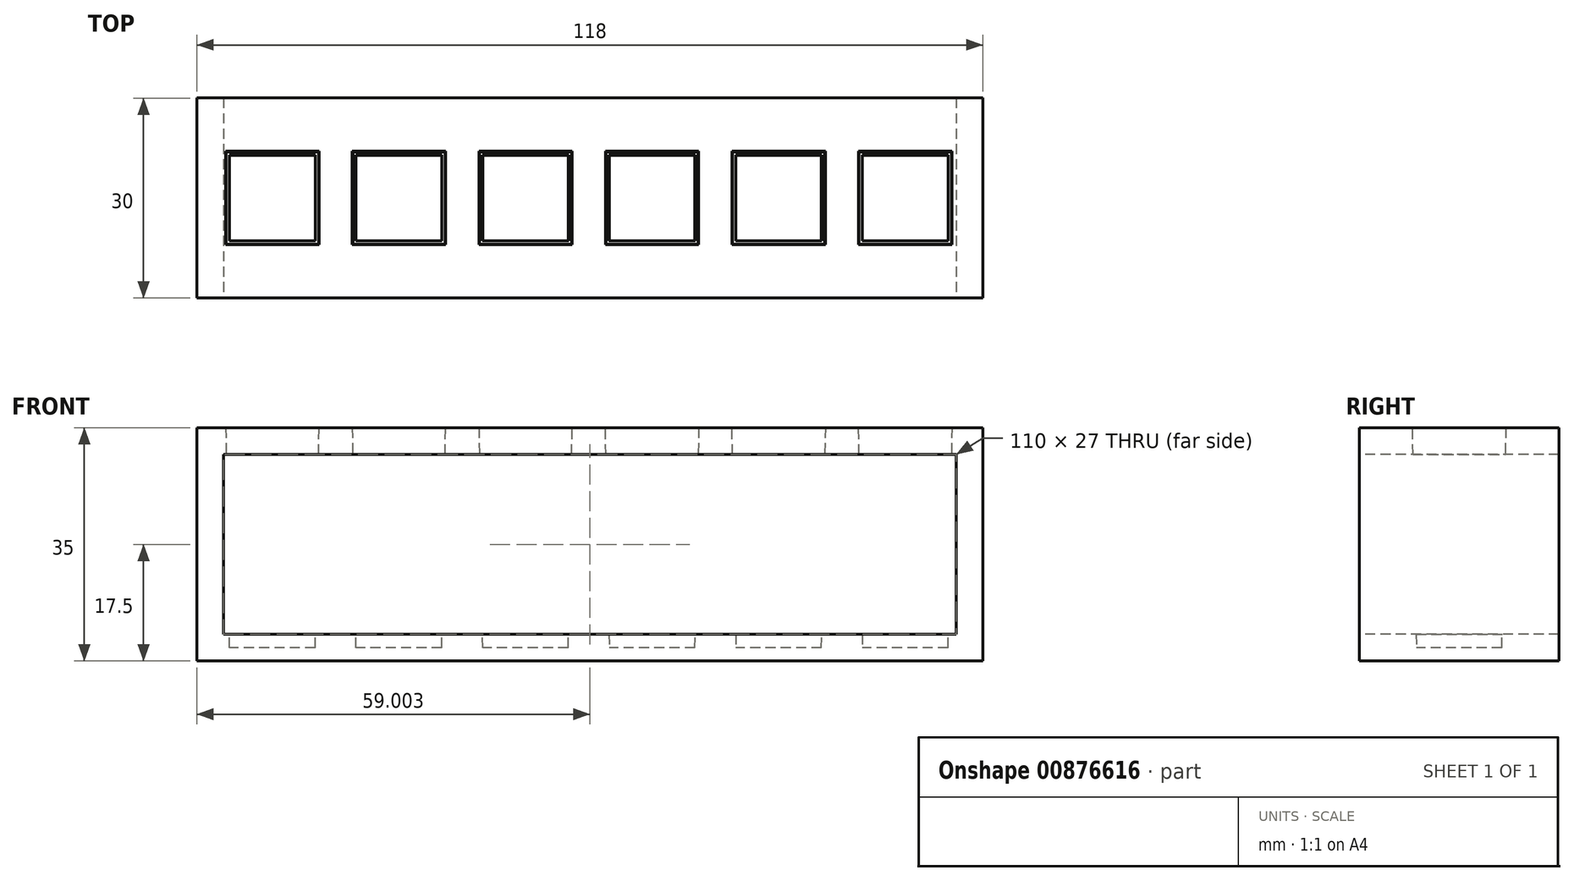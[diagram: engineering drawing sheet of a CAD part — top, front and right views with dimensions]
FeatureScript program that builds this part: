
annotation { "Feature Type Name" : "Feature", "Feature Type Description" : "" }
export const myFeature = defineFeature(function(context is Context, id is Id, definition is map)
    precondition{}
    {
        {
            var Q0;
            Q0=qCreatedBy(makeId("Top.planeOp"),FACE);
            var sketch = newSketch(context, id + "F0", { "sketchPlane" : qUnion([Q0])});
            skLineSegment(sketch, "E0.bottom", {"start": v(-64.3, -10.83) * mm, "end": v(53.7, -10.83) * mm});
            skLineSegment(sketch, "E0.top", {"start": v(-64.3, -40.83) * mm, "end": v(53.7, -40.83) * mm});
            skLineSegment(sketch, "E0.left", {"start": v(-64.3, -10.83) * mm, "end": v(-64.3, -40.83) * mm});
            skLineSegment(sketch, "E0.right", {"start": v(53.7, -10.83) * mm, "end": v(53.7, -40.83) * mm});
            skSolve(sketch);
        }
        {
            var Q0;
            Q0 = qSketchRegion(id + "F0", true);
            extrude(context, id + "F1", {"entities" : qUnion([Q0]), "depth" : 35 * mm, "offsetDistance" : 25 * mm});
        }
        {
            var Q0;
            Q0=makeQuery(id+"F1.opExtrude","CAP_FACE",FACE,{"disambiguationData":[OSD([sQuery(id+"F0.wireOp",EDGE,"E0.bottom"),sQuery(id+"F0.wireOp",EDGE,"E0.top"),sQuery(id+"F0.wireOp",EDGE,"E0.left"),sQuery(id+"F0.wireOp",EDGE,"E0.right")])],"isStart":false});
            var sketch = newSketch(context, id + "F2", { "sketchPlane" : qUnion([Q0])});
            skLineSegment(sketch, "E1.bottom", {"start": v(-59.96, -18.83) * mm, "end": v(-45.96, -18.83) * mm});
            skLineSegment(sketch, "E1.top", {"start": v(-59.96, -32.83) * mm, "end": v(-45.96, -32.83) * mm});
            skLineSegment(sketch, "E1.left", {"start": v(-59.96, -18.83) * mm, "end": v(-59.96, -32.83) * mm});
            skLineSegment(sketch, "E1.right", {"start": v(-45.96, -18.83) * mm, "end": v(-45.96, -32.83) * mm});
            skLineSegment(sketch, "E2.bottom", {"start": v(-40.96, -18.83) * mm, "end": v(-26.96, -18.83) * mm});
            skLineSegment(sketch, "E2.top", {"start": v(-40.96, -32.83) * mm, "end": v(-26.96, -32.83) * mm});
            skLineSegment(sketch, "E2.left", {"start": v(-40.96, -18.83) * mm, "end": v(-40.96, -32.83) * mm});
            skLineSegment(sketch, "E2.right", {"start": v(-26.96, -18.83) * mm, "end": v(-26.96, -32.83) * mm});
            skLineSegment(sketch, "E3.bottom", {"start": v(-21.96, -18.83) * mm, "end": v(-7.96, -18.83) * mm});
            skLineSegment(sketch, "E3.top", {"start": v(-21.96, -32.83) * mm, "end": v(-7.96, -32.83) * mm});
            skLineSegment(sketch, "E3.left", {"start": v(-21.96, -18.83) * mm, "end": v(-21.96, -32.83) * mm});
            skLineSegment(sketch, "E3.right", {"start": v(-7.96, -18.83) * mm, "end": v(-7.96, -32.83) * mm});
            skLineSegment(sketch, "E4.bottom", {"start": v(11.04, -18.83) * mm, "end": v(-2.96, -18.83) * mm});
            skLineSegment(sketch, "E4.top", {"start": v(11.04, -32.83) * mm, "end": v(-2.96, -32.83) * mm});
            skLineSegment(sketch, "E4.left", {"start": v(11.04, -18.83) * mm, "end": v(11.04, -32.83) * mm});
            skLineSegment(sketch, "E4.right", {"start": v(-2.96, -18.83) * mm, "end": v(-2.96, -32.83) * mm});
            skLineSegment(sketch, "E5.bottom", {"start": v(30.04, -18.83) * mm, "end": v(16.04, -18.83) * mm});
            skLineSegment(sketch, "E5.top", {"start": v(30.04, -32.83) * mm, "end": v(16.04, -32.83) * mm});
            skLineSegment(sketch, "E5.left", {"start": v(30.04, -18.83) * mm, "end": v(30.04, -32.83) * mm});
            skLineSegment(sketch, "E5.right", {"start": v(16.04, -18.83) * mm, "end": v(16.04, -32.83) * mm});
            skLineSegment(sketch, "E6.bottom", {"start": v(49.04, -18.83) * mm, "end": v(35.04, -18.83) * mm});
            skLineSegment(sketch, "E6.top", {"start": v(49.04, -32.83) * mm, "end": v(35.04, -32.83) * mm});
            skLineSegment(sketch, "E6.left", {"start": v(49.04, -18.83) * mm, "end": v(49.04, -32.83) * mm});
            skLineSegment(sketch, "E6.right", {"start": v(35.04, -18.83) * mm, "end": v(35.04, -32.83) * mm});
            skSolve(sketch);
        }
        {
            var Q0;
            Q0 = qSketchRegion(id + "F2", true);
            extrude(context, id + "F3", {"entities" : qUnion([Q0]), "operationType" : NewBodyOperationType.REMOVE, "oppositeDirection" : true, "depth" : 33 * mm, "offsetDistance" : 25 * mm, "hasDraft" : true, "draftAngle" : 1 * degree, "draftPullDirection" : true});
        }
        {
            var Q0;
            Q0=makeQuery(id+"F1.opExtrude","SWEPT_FACE",FACE,{"disambiguationData":[OSD([sQuery(id+"F0.wireOp",EDGE,"E0.top")])]});
            var sketch = newSketch(context, id + "F4", { "sketchPlane" : qUnion([Q0])});
            skLineSegment(sketch, "E7.bottom", {"start": v(-60.3, 31) * mm, "end": v(49.7, 31) * mm});
            skLineSegment(sketch, "E7.top", {"start": v(-60.3, 4) * mm, "end": v(49.7, 4) * mm});
            skLineSegment(sketch, "E7.left", {"start": v(-60.3, 31) * mm, "end": v(-60.3, 4) * mm});
            skLineSegment(sketch, "E7.right", {"start": v(49.7, 31) * mm, "end": v(49.7, 4) * mm});
            skSolve(sketch);
        }
        {
            var Q0;
            Q0 = qSketchRegion(id + "F4", true);
            extrude(context, id + "F5", {"entities" : qUnion([Q0]), "operationType" : NewBodyOperationType.REMOVE, "oppositeDirection" : true, "depth" : 30 * mm, "offsetDistance" : 25 * mm});
        }
    });
